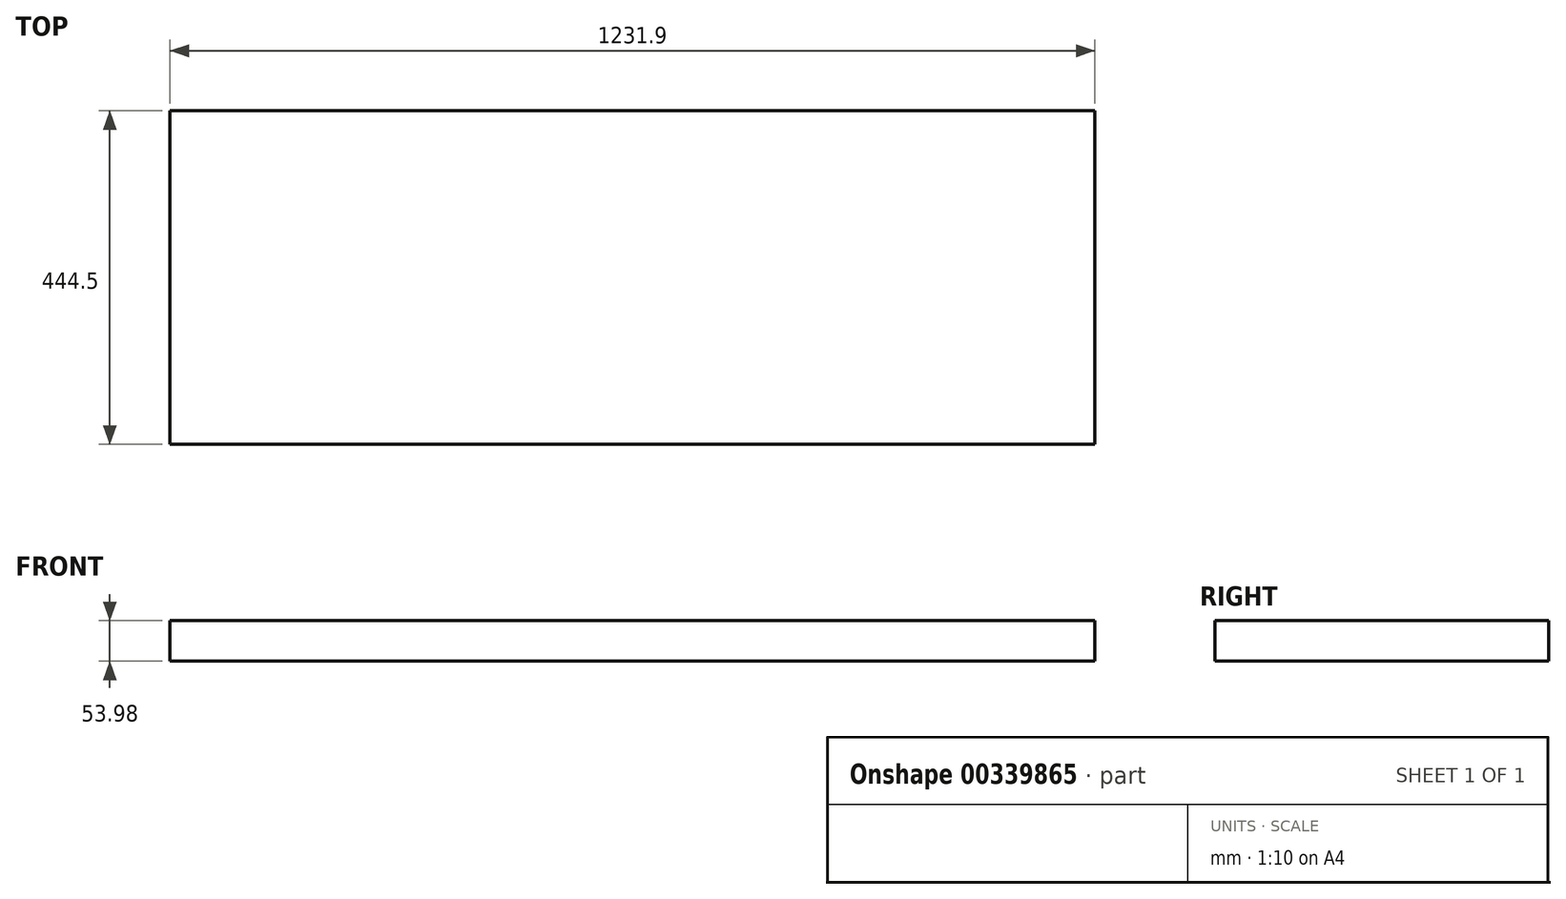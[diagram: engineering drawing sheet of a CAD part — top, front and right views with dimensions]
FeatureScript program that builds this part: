
annotation { "Feature Type Name" : "Feature", "Feature Type Description" : "" }
export const myFeature = defineFeature(function(context is Context, id is Id, definition is map)
    precondition{}
    {
        {
            var Q0;
            Q0=qCreatedBy(makeId("Top.planeOp"),FACE);
            var sketch = newSketch(context, id + "F0", { "sketchPlane" : qUnion([Q0])});
            skLineSegment(sketch, "E0.bottom", {"start": v(-602.13, 213.02) * mm, "end": v(629.77, 213.02) * mm});
            skLineSegment(sketch, "E0.top", {"start": v(-602.13, -231.48) * mm, "end": v(629.77, -231.48) * mm});
            skLineSegment(sketch, "E0.left", {"start": v(-602.13, 213.02) * mm, "end": v(-602.13, -231.48) * mm});
            skLineSegment(sketch, "E0.right", {"start": v(629.77, 213.02) * mm, "end": v(629.77, -231.48) * mm});
            skSolve(sketch);
        }
        {
            var Q0;
            Q0=makeQuery(id+"F0.imprint","IMPRINT",FACE,{"disambiguationData":[TD([[makeQuery(id+"F0.imprint","IMPRINT",EDGE,{"derivedFrom":sQuery(id+"F0.wireOp",EDGE,"E0.bottom")}),-1.0]])]});
            extrude(context, id + "F1", {"entities" : qUnion([Q0]), "depth" : 53.97 * mm, "offsetDistance" : 25.4 * mm});
        }
    });
